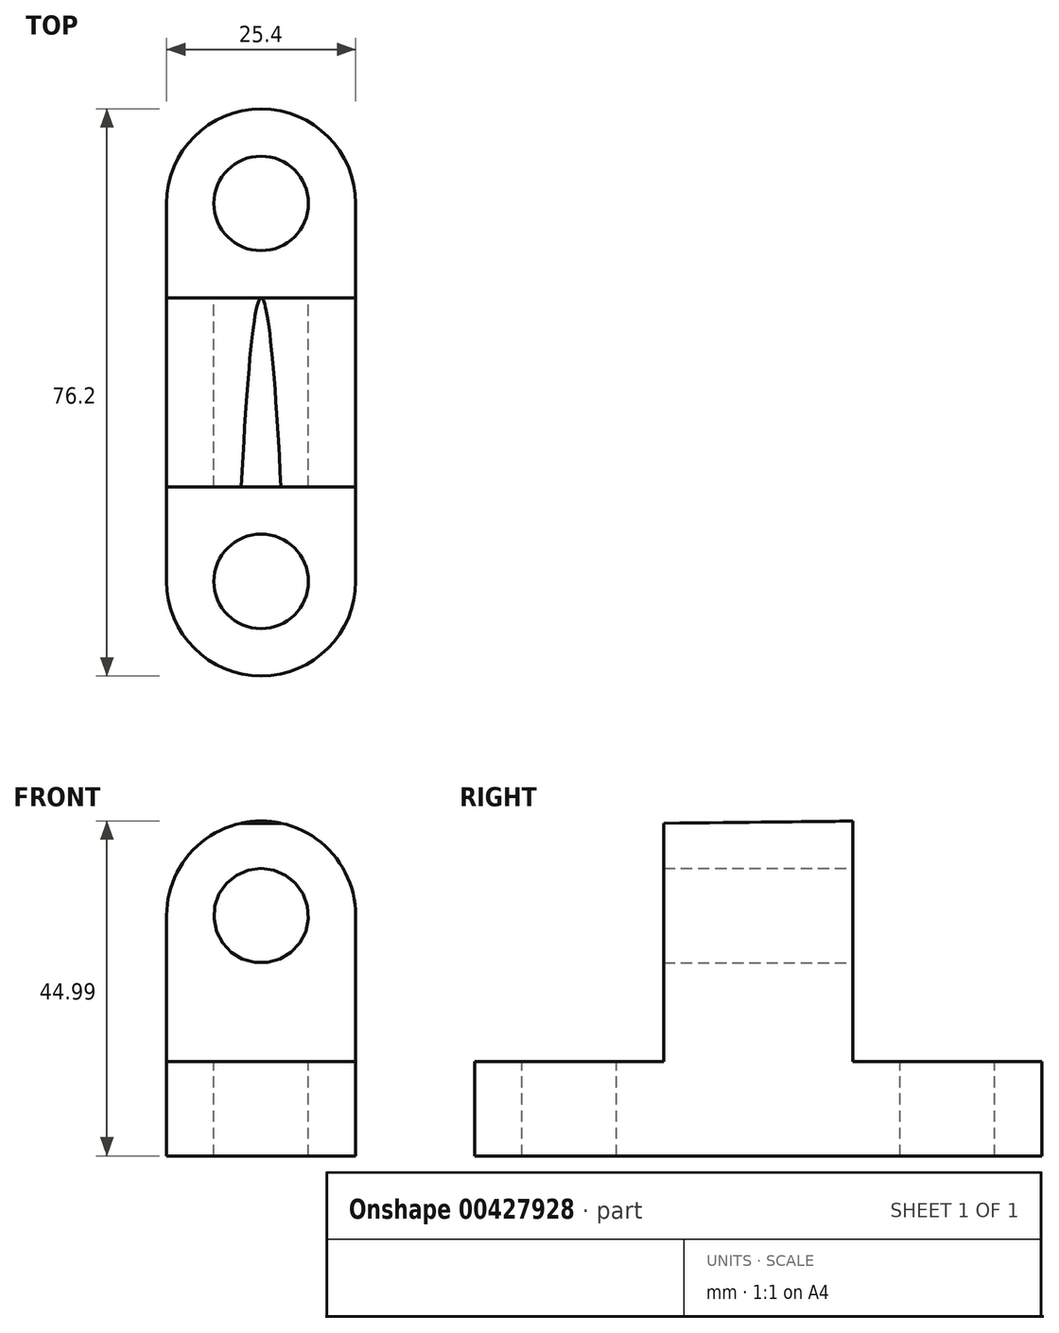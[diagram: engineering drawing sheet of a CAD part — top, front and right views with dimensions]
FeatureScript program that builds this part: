
annotation { "Feature Type Name" : "Feature", "Feature Type Description" : "" }
export const myFeature = defineFeature(function(context is Context, id is Id, definition is map)
    precondition{}
    {
        {
            var Q0;
            Q0=qCreatedBy(makeId("Right.planeOp"),FACE);
            var sketch = newSketch(context, id + "F0", { "sketchPlane" : qUnion([Q0])});
            skLineSegment(sketch, "E0", {"start": v(-6.35, 12.7) * mm, "end": v(19.05, 12.7) * mm});
            skLineSegment(sketch, "E1", {"start": v(19.05, 12.7) * mm, "end": v(19.05, 44.7) * mm});
            skLineSegment(sketch, "E2", {"start": v(44.45, 44.99) * mm, "end": v(44.45, 12.7) * mm});
            skLineSegment(sketch, "E3", {"start": v(44.45, 12.7) * mm, "end": v(69.85, 12.7) * mm});
            skLineSegment(sketch, "E4", {"start": v(69.85, 12.7) * mm, "end": v(69.85, 0) * mm});
            skLineSegment(sketch, "E5", {"start": v(69.85, 0) * mm, "end": v(0, 0) * mm});
            skLineSegment(sketch, "E6", {"start": v(19.05, 44.7) * mm, "end": v(44.45, 44.99) * mm});
            skLineSegment(sketch, "E7", {"start": v(-6.35, 12.7) * mm, "end": v(-6.35, 0) * mm});
            skLineSegment(sketch, "E8", {"start": v(-6.35, 0) * mm, "end": v(0, 0) * mm});
            skSolve(sketch);
        }
        {
            var Q0;
            Q0=makeQuery(id+"F0.imprint","IMPRINT",FACE,{"disambiguationData":[TD([[makeQuery(id+"F0.imprint","IMPRINT",EDGE,{"derivedFrom":sQuery(id+"F0.wireOp",EDGE,"E0")}),-1.0]])]});
            extrude(context, id + "F1", {"entities" : qUnion([Q0]), "depth" : 25.4 * mm});
        }
        {
            var Q0;
            Q0=makeQuery(id+"F1.opExtrude","SWEPT_FACE",FACE,{"disambiguationData":[OSD([sQuery(id+"F0.wireOp",EDGE,"E2")])]});
            var sketch = newSketch(context, id + "F2", { "sketchPlane" : qUnion([Q0])});
            skArc(sketch, "E9", {"start": v(0, 32.29) * mm, "mid": v(-12.7, 44.99) * mm, "end": v(-25.4, 32.29) * mm});
            skCircle(sketch, "E10", {"center": v(-12.7, 32.29) * mm, "radius": 6.35 * mm});
            skSolve(sketch);
        }
        {
            var Q0;
            {var subQ0=sQuery(id+"F2.wireOp",EDGE,"E9");var subQ1=sQuery(id+"F0.wireOp",EDGE,"E2");var subQ2=makeQuery(id+"F1.opExtrude","CAP_EDGE",EDGE,{"disambiguationData":[OSD([subQ1])],"isStart":false});var subQ3=makeQuery(id+"F2.imprint","INTERSECT",VERTEX,{"derivedFrom":[subQ2,subQ0]});Q0=makeQuery(id+"F2.imprint","IMPRINT",FACE,{"disambiguationData":[TD([[makeQuery(id+"F2.imprint","IMPRINT",EDGE,{"disambiguationData":[TD([[subQ3,1.0]])],"derivedFrom":subQ0}),-1.0]])]});}
            var Q1;
            {var subQ0=sQuery(id+"F2.wireOp",EDGE,"E9");var subQ1=sQuery(id+"F0.wireOp",EDGE,"E2");var subQ2=makeQuery(id+"F1.opExtrude","CAP_EDGE",EDGE,{"disambiguationData":[OSD([subQ1])],"isStart":true});var subQ3=makeQuery(id+"F2.imprint","INTERSECT",VERTEX,{"derivedFrom":[subQ2,subQ0]});Q1=makeQuery(id+"F2.imprint","IMPRINT",FACE,{"disambiguationData":[TD([[makeQuery(id+"F2.imprint","IMPRINT",EDGE,{"disambiguationData":[TD([[subQ3,-1.0]])],"derivedFrom":subQ0}),-1.0]])]});}
            var Q2;
            Q2=makeQuery(id+"F2.imprint","IMPRINT",FACE,{"disambiguationData":[TD([[makeQuery(id+"F2.imprint","IMPRINT",EDGE,{"derivedFrom":sQuery(id+"F2.wireOp",EDGE,"E10")}),1.0]])]});
            extrude(context, id + "F3", {"entities" : qUnion([Q0, Q1, Q2]), "operationType" : NewBodyOperationType.REMOVE, "oppositeDirection" : true, "depth" : 25.4 * mm});
        }
        {
            var Q0;
            Q0=makeQuery(id+"F1.opExtrude","SWEPT_FACE",FACE,{"disambiguationData":[OSD([sQuery(id+"F0.wireOp",EDGE,"E3")])]});
            var sketch = newSketch(context, id + "F4", { "sketchPlane" : qUnion([Q0])});
            skArc(sketch, "E11", {"start": v(25.4, 57.15) * mm, "mid": v(12.7, 69.85) * mm, "end": v(0, 57.15) * mm});
            skCircle(sketch, "E12", {"center": v(12.7, 57.15) * mm, "radius": 6.35 * mm});
            skSolve(sketch);
        }
        {
            var Q0;
            Q0=makeQuery(id+"F4.imprint","IMPRINT",FACE,{"disambiguationData":[TD([[makeQuery(id+"F4.imprint","IMPRINT",EDGE,{"derivedFrom":sQuery(id+"F4.wireOp",EDGE,"E12")}),1.0]])]});
            var Q1;
            {var subQ0=sQuery(id+"F4.wireOp",EDGE,"E11");var subQ1=sQuery(id+"F0.wireOp",EDGE,"E3");var subQ2=makeQuery(id+"F1.opExtrude","CAP_EDGE",EDGE,{"disambiguationData":[OSD([subQ1])],"isStart":false});var subQ3=makeQuery(id+"F4.imprint","INTERSECT",VERTEX,{"derivedFrom":[subQ2,subQ0]});Q1=makeQuery(id+"F4.imprint","IMPRINT",FACE,{"disambiguationData":[TD([[makeQuery(id+"F4.imprint","IMPRINT",EDGE,{"disambiguationData":[TD([[subQ3,-1.0]])],"derivedFrom":subQ0}),-1.0]])]});}
            var Q2;
            {var subQ0=sQuery(id+"F4.wireOp",EDGE,"E11");var subQ1=sQuery(id+"F0.wireOp",EDGE,"E3");var subQ2=makeQuery(id+"F1.opExtrude","CAP_EDGE",EDGE,{"disambiguationData":[OSD([subQ1])],"isStart":true});var subQ3=makeQuery(id+"F4.imprint","INTERSECT",VERTEX,{"derivedFrom":[subQ2,subQ0]});Q2=makeQuery(id+"F4.imprint","IMPRINT",FACE,{"disambiguationData":[TD([[makeQuery(id+"F4.imprint","IMPRINT",EDGE,{"disambiguationData":[TD([[subQ3,1.0]])],"derivedFrom":subQ0}),-1.0]])]});}
            extrude(context, id + "F5", {"entities" : qUnion([Q0, Q1, Q2]), "operationType" : NewBodyOperationType.REMOVE, "oppositeDirection" : true, "depth" : 12.7 * mm});
        }
        {
            var Q0;
            Q0=makeQuery(id+"F1.opExtrude","SWEPT_FACE",FACE,{"disambiguationData":[OSD([sQuery(id+"F0.wireOp",EDGE,"E0")])]});
            var sketch = newSketch(context, id + "F6", { "sketchPlane" : qUnion([Q0])});
            skArc(sketch, "E13", {"start": v(0, 6.35) * mm, "mid": v(12.7, -6.35) * mm, "end": v(25.4, 6.35) * mm});
            skCircle(sketch, "E14", {"center": v(12.7, 6.35) * mm, "radius": 6.35 * mm});
            skSolve(sketch);
        }
        {
            var Q0;
            Q0=makeQuery(id+"F6.imprint","IMPRINT",FACE,{"disambiguationData":[TD([[makeQuery(id+"F6.imprint","IMPRINT",EDGE,{"derivedFrom":sQuery(id+"F6.wireOp",EDGE,"E14")}),1.0]])]});
            var Q1;
            {var subQ0=sQuery(id+"F6.wireOp",EDGE,"E13");var subQ1=sQuery(id+"F0.wireOp",EDGE,"E0");var subQ2=makeQuery(id+"F1.opExtrude","CAP_EDGE",EDGE,{"disambiguationData":[OSD([subQ1])],"isStart":false});var subQ3=makeQuery(id+"F6.imprint","INTERSECT",VERTEX,{"derivedFrom":[subQ2,subQ0]});Q1=makeQuery(id+"F6.imprint","IMPRINT",FACE,{"disambiguationData":[TD([[makeQuery(id+"F6.imprint","IMPRINT",EDGE,{"disambiguationData":[TD([[subQ3,1.0]])],"derivedFrom":subQ0}),-1.0]])]});}
            var Q2;
            {var subQ0=sQuery(id+"F6.wireOp",EDGE,"E13");var subQ1=sQuery(id+"F0.wireOp",EDGE,"E0");var subQ2=makeQuery(id+"F1.opExtrude","CAP_EDGE",EDGE,{"disambiguationData":[OSD([subQ1])],"isStart":true});var subQ3=makeQuery(id+"F6.imprint","INTERSECT",VERTEX,{"derivedFrom":[subQ2,subQ0]});Q2=makeQuery(id+"F6.imprint","IMPRINT",FACE,{"disambiguationData":[TD([[makeQuery(id+"F6.imprint","IMPRINT",EDGE,{"disambiguationData":[TD([[subQ3,-1.0]])],"derivedFrom":subQ0}),-1.0]])]});}
            extrude(context, id + "F7", {"entities" : qUnion([Q0, Q1, Q2]), "operationType" : NewBodyOperationType.REMOVE, "oppositeDirection" : true, "depth" : 12.7 * mm});
        }
    });
